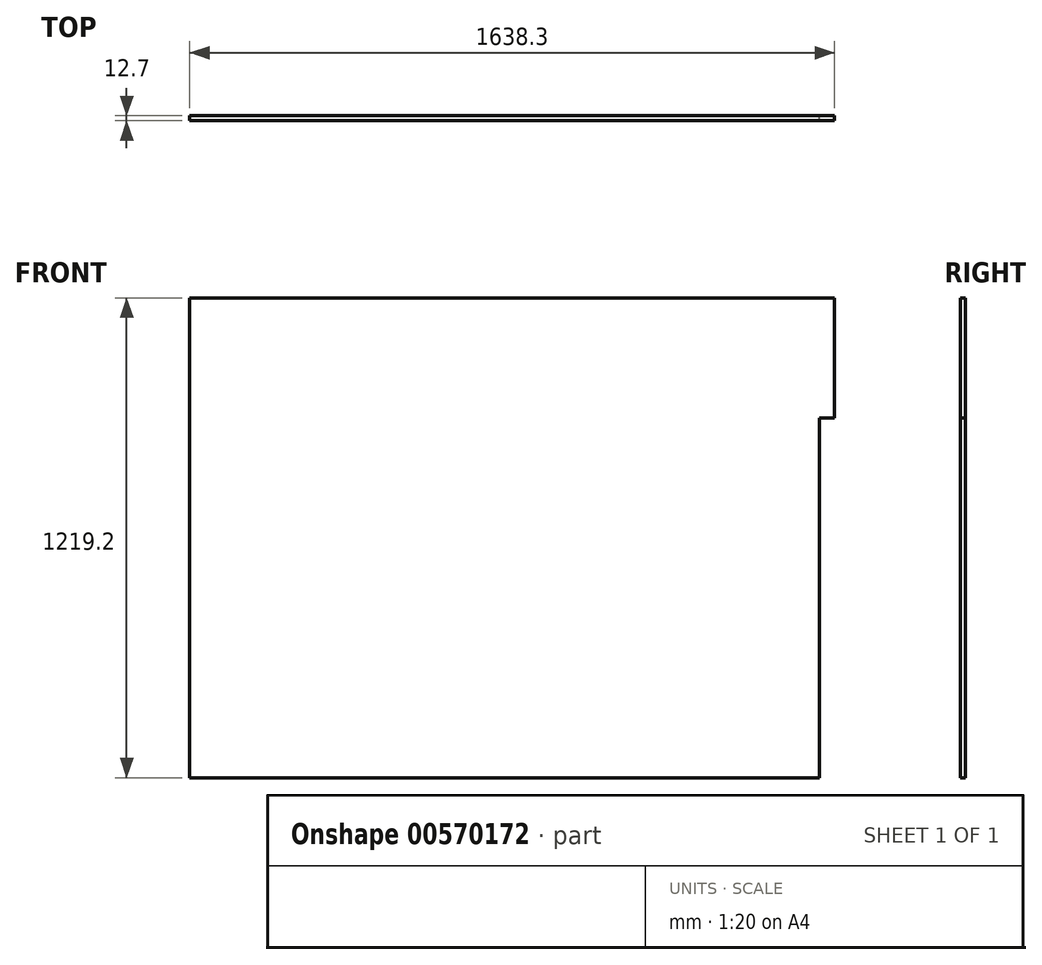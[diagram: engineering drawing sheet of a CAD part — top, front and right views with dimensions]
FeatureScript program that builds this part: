
annotation { "Feature Type Name" : "Feature", "Feature Type Description" : "" }
export const myFeature = defineFeature(function(context is Context, id is Id, definition is map)
    precondition{}
    {
        {
            var Q0;
            Q0=qCreatedBy(makeId("Front.planeOp"),FACE);
            var sketch = newSketch(context, id + "F0", { "sketchPlane" : qUnion([Q0])});
            skLineSegment(sketch, "E0.bottom", {"start": v(0, 0) * mm, "end": v(1600.2, 0) * mm});
            skLineSegment(sketch, "E0.top", {"start": v(0, 1219.2) * mm, "end": v(1638.3, 1219.2) * mm});
            skLineSegment(sketch, "E0.left", {"start": v(0, 0) * mm, "end": v(0, 1219.2) * mm});
            skLineSegment(sketch, "E1", {"start": v(1638.3, 1219.2) * mm, "end": v(1638.3, 914.4) * mm});
            skLineSegment(sketch, "E2", {"start": v(1638.3, 914.4) * mm, "end": v(1600.2, 914.4) * mm});
            skLineSegment(sketch, "E3", {"start": v(1600.2, 914.4) * mm, "end": v(1600.2, 0) * mm});
            skSolve(sketch);
        }
        {
            var Q0;
            Q0 = qSketchRegion(id + "F0", true);
            extrude(context, id + "F1", {"entities" : qUnion([Q0]), "depth" : 12.7 * mm, "offsetDistance" : 25.4 * mm});
        }
    });
